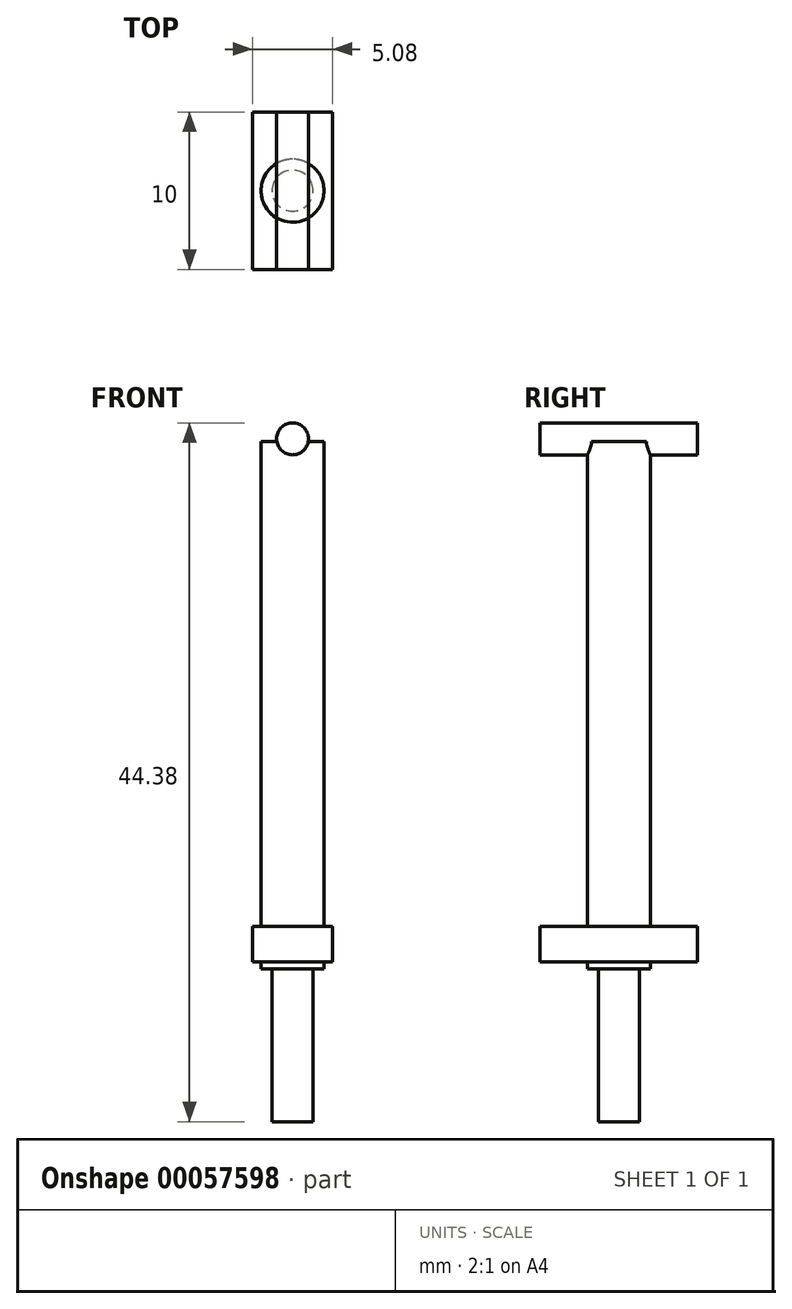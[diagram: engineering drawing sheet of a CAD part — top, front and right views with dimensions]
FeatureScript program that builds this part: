
annotation { "Feature Type Name" : "Feature", "Feature Type Description" : "" }
export const myFeature = defineFeature(function(context is Context, id is Id, definition is map)
    precondition{}
    {
        {
            var Q0;
            Q0=qCreatedBy(makeId("Top.planeOp"),FACE);
            var sketch = newSketch(context, id + "F0", { "sketchPlane" : qUnion([Q0])});
            skCircle(sketch, "E0", {"center": v(0, 0) * mm, "radius": 2 * mm});
            skSolve(sketch);
        }
        {
            var Q0;
            Q0 = qSketchRegion(id + "F0", true);
            extrude(context, id + "F1", {"entities" : qUnion([Q0]), "depth" : 33.5 * mm});
        }
        {
            var Q0;
            Q0=makeQuery(id+"F1.opExtrude","CAP_FACE",FACE,{"disambiguationData":[OSD([sQuery(id+"F0.wireOp",EDGE,"E0")])],"isStart":true});
            var sketch = newSketch(context, id + "F2", { "sketchPlane" : qUnion([Q0])});
            skCircle(sketch, "E1", {"center": v(0, 0) * mm, "radius": 1.3 * mm});
            skSolve(sketch);
        }
        {
            var Q0;
            Q0 = qSketchRegion(id + "F2", true);
            extrude(context, id + "F3", {"entities" : qUnion([Q0]), "operationType" : NewBodyOperationType.ADD, "depth" : 9.7 * mm});
        }
        {
            var Q0;
            Q0=qCreatedBy(makeId("Front.planeOp"),FACE);
            var sketch = newSketch(context, id + "F4", { "sketchPlane" : qUnion([Q0])});
            skLineSegment(sketch, "E2.bottom", {"start": v(-2.54, 2.69) * mm, "end": v(2.54, 2.69) * mm});
            skLineSegment(sketch, "E2.top", {"start": v(-2.54, 0.43) * mm, "end": v(2.54, 0.43) * mm});
            skLineSegment(sketch, "E2.left", {"start": v(-2.54, 2.69) * mm, "end": v(-2.54, 0.43) * mm});
            skLineSegment(sketch, "E2.right", {"start": v(2.54, 2.69) * mm, "end": v(2.54, 0.43) * mm});
            skPoint(sketch, "E2.middle", {"position": v(0, 1.56) * mm});
            skCircle(sketch, "E3", {"center": v(0, 33.67) * mm, "radius": 1.01 * mm});
            skSolve(sketch);
        }
        {
            var Q0;
            Q0 = qSketchRegion(id + "F4", true);
            extrude(context, id + "F5", {"entities" : qUnion([Q0]), "operationType" : NewBodyOperationType.ADD, "endBound" : BoundingType.SYMMETRIC, "depth" : 10 * mm});
        }
    });
